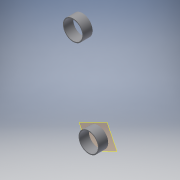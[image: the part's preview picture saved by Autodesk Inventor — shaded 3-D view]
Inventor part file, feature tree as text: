
AUTODESK INVENTOR PART (.ipt)
format: ipt  version: 2019 (Build 230136000, 136)  size: 107,520 bytes
history: native  units: mm
features: other x4, extrude x2, sketch x2, reference x2, plane x1
ambient origin geometry x8: Origin, YZ Plane, XZ Plane, XY Plane, X Axis, Y Axis, Z Axis, Center Point
bodies: Solid1 (feature_tree)
feature tree (11):
  extrude  "Extrusion1"  Depth=4.0mm TaperAngle=0.0deg
  plane  "Work Plane1"
  extrude  "Extrusion2"  [1 undecoded]
  sketch  "Sketch1"  dims[d0=4.0mm d1=0.0mm d3=4.0mm d4=0.0mm]
  reference  "Reference1"
  sketch  "Sketch2"
  reference  "Reference2"
  parser-record x1  (decoder bookkeeping rows leaked as tree rows — omitted from the tree; the rows remain in map.json)
  other  "mount assem.iam"
  other  "94695A250_TYPE 316 STAINLESS STEEL COUNTERSUNK WASHER:2"
  other  "94695A250_TYPE 316 STAINLESS STEEL COUNTERSUNK WASHER:1"
note: 1 required parameter value undecoded (feature->parameter linkage not recoverable at this tier; creation-order binding heuristic only, values carry confidence <= 0.55)
note: 1 file-system path scrubbed to <path> (originals preserved in map.json)
